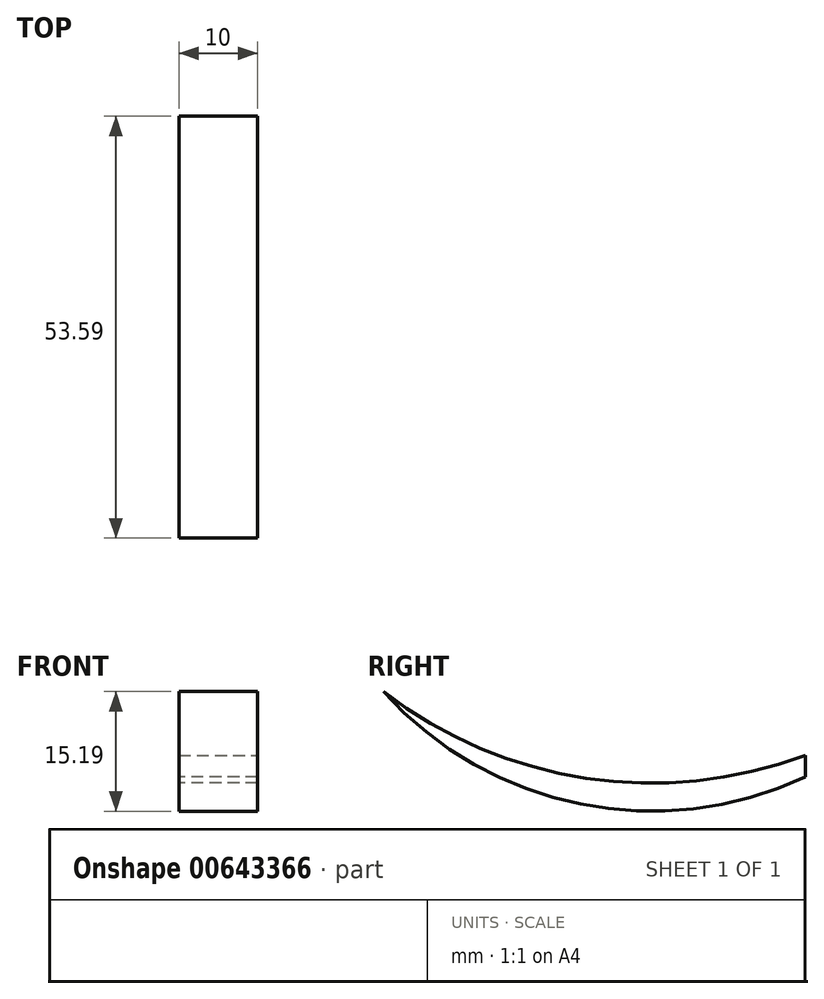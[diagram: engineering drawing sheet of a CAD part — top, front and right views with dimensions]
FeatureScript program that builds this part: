
annotation { "Feature Type Name" : "Feature", "Feature Type Description" : "" }
export const myFeature = defineFeature(function(context is Context, id is Id, definition is map)
    precondition{}
    {
        {
            var Q0;
            Q0=qCreatedBy(makeId("Right.planeOp"),FACE);
            var sketch = newSketch(context, id + "F0", { "sketchPlane" : qUnion([Q0])});
            skArc(sketch, "E0", {"start": v(-68.08, 0) * mm, "mid": v(-34.04, -15.2) * mm, "end": v(0, 0) * mm});
            skArc(sketch, "E1", {"start": v(-68.08, 0) * mm, "mid": v(-34.04, -11.61) * mm, "end": v(0, 0) * mm});
            skLineSegment(sketch, "E2", {"start": v(0, 0) * mm, "end": v(0, -10.8) * mm});
            skLineSegment(sketch, "E3", {"start": v(0, -10.8) * mm, "end": v(-14.5, -10.8) * mm});
            skSolve(sketch);
        }
        {
            var Q0;
            {var subQ0=sQuery(id+"F0.wireOp",EDGE,"E1");Q0=makeQuery(id+"F0.imprint","IMPRINT",FACE,{"disambiguationData":[TD([[makeQuery(id+"F0.imprint","IMPRINT",EDGE,{"derivedFrom":subQ0}),-1.0]])]});}
            var Q1;
            {var subQ0=sQuery(id+"F0.wireOp",EDGE,"E2");Q1=makeQuery(id+"F0.imprint","IMPRINT",FACE,{"disambiguationData":[TD([[makeQuery(id+"F0.imprint","IMPRINT",EDGE,{"derivedFrom":subQ0}),-1.0]])]});}
            extrude(context, id + "F1", {"entities" : qUnion([Q0, Q1]), "depth" : 10 * mm, "offsetDistance" : 25 * mm});
        }
        {
            var Q0;
            Q0=makeQuery(id+"F1.opExtrude","CAP_FACE",FACE,{"disambiguationData":[OSD([sQuery(id+"F0.wireOp",EDGE,"E0"),sQuery(id+"F0.wireOp",EDGE,"E1"),sQuery(id+"F0.wireOp",EDGE,"E2"),sQuery(id+"F0.wireOp",EDGE,"E3")])],"isStart":true});
            var sketch = newSketch(context, id + "F2", { "sketchPlane" : qUnion([Q0])});
            skLineSegment(sketch, "E4", {"start": v(14.5, -10.8) * mm, "end": v(14.5, -8.07) * mm});
            skSolve(sketch);
        }
        {
            var Q0;
            {var subQ0=sQuery(id+"F2.wireOp",EDGE,"E4");Q0=makeQuery(id+"F2.imprint","IMPRINT",FACE,{"disambiguationData":[TD([[makeQuery(id+"F2.imprint","IMPRINT",EDGE,{"derivedFrom":subQ0}),1.0]])]});}
            extrude(context, id + "F3", {"entities" : qUnion([Q0]), "operationType" : NewBodyOperationType.ADD, "depth" : 35 * mm, "offsetDistance" : 25 * mm});
        }
        {
            var Q0;
            Q0=makeQuery(id+"F1.opExtrude","CAP_FACE",FACE,{"disambiguationData":[OSD([sQuery(id+"F0.wireOp",EDGE,"E0"),sQuery(id+"F0.wireOp",EDGE,"E1"),sQuery(id+"F0.wireOp",EDGE,"E2"),sQuery(id+"F0.wireOp",EDGE,"E3")])],"isStart":false});
            var sketch = newSketch(context, id + "F4", { "sketchPlane" : qUnion([Q0])});
            skLineSegment(sketch, "E5", {"start": v(-14.5, -10.8) * mm, "end": v(-14.5, -8.07) * mm});
            skSolve(sketch);
        }
        {
            var Q0;
            {var subQ0=sQuery(id+"F4.wireOp",EDGE,"E5");Q0=makeQuery(id+"F4.imprint","IMPRINT",FACE,{"disambiguationData":[TD([[makeQuery(id+"F4.imprint","IMPRINT",EDGE,{"derivedFrom":subQ0}),-1.0]])]});}
            extrude(context, id + "F5", {"entities" : qUnion([Q0]), "operationType" : NewBodyOperationType.REMOVE, "endBound" : BoundingType.THROUGH_ALL, "oppositeDirection" : true, "depth" : 25 * mm, "offsetDistance" : 25 * mm});
        }
    });
